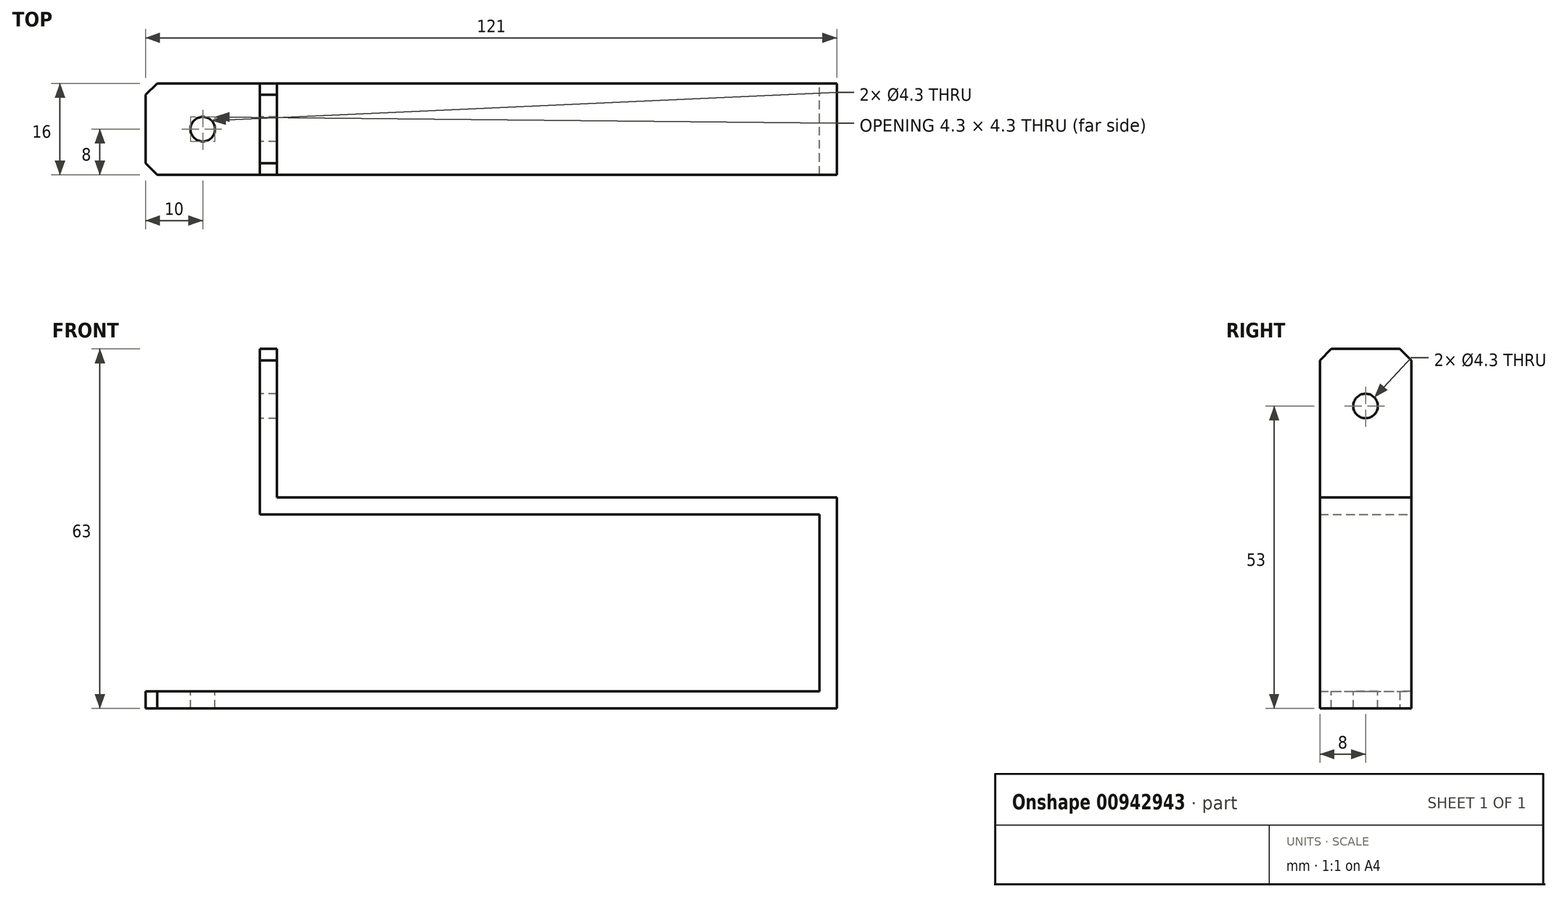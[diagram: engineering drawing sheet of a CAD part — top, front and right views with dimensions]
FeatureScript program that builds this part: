
annotation { "Feature Type Name" : "Feature", "Feature Type Description" : "" }
export const myFeature = defineFeature(function(context is Context, id is Id, definition is map)
    precondition{}
    {
        {
            var Q0;
            Q0=qCreatedBy(makeId("Front.planeOp"),FACE);
            var sketch = newSketch(context, id + "F0", { "sketchPlane" : qUnion([Q0])});
            skLineSegment(sketch, "E0", {"start": v(0, 0) * mm, "end": v(-20, 0) * mm});
            skLineSegment(sketch, "E1", {"start": v(0, 0) * mm, "end": v(0, 60) * mm, "construction": true});
            skPoint(sketch, "E2", {"position": v(-10, 0) * mm});
            skPoint(sketch, "E3", {"position": v(0, 50) * mm});
            skLineSegment(sketch, "E4", {"start": v(0, 0) * mm, "end": v(0, 31) * mm, "construction": true});
            skLineSegment(sketch, "E5", {"start": v(0, 31) * mm, "end": v(98, 31) * mm});
            skLineSegment(sketch, "E6", {"start": v(98, 31) * mm, "end": v(98, 0) * mm});
            skLineSegment(sketch, "E7", {"start": v(98, 0) * mm, "end": v(0, 0) * mm});
            skLineSegment(sketch, "E8.0", {"start": v(101, -3) * mm, "end": v(0, -3) * mm});
            skLineSegment(sketch, "E8.1", {"start": v(101, 34) * mm, "end": v(101, -3) * mm});
            skLineSegment(sketch, "E8.2", {"start": v(3, 34) * mm, "end": v(101, 34) * mm});
            skLineSegment(sketch, "E9", {"start": v(0, -3) * mm, "end": v(-20, -3) * mm});
            skLineSegment(sketch, "E10", {"start": v(-20, -3) * mm, "end": v(-20, 0) * mm});
            skLineSegment(sketch, "E11", {"start": v(3, 34) * mm, "end": v(3, 60) * mm});
            skLineSegment(sketch, "E12", {"start": v(3, 60) * mm, "end": v(0, 60) * mm});
            skLineSegment(sketch, "E13", {"start": v(0, 31) * mm, "end": v(0, 60) * mm});
            skSolve(sketch);
        }
        {
            var Q0;
            Q0 = qSketchRegion(id + "F0", true);
            extrude(context, id + "F1", {"entities" : qUnion([Q0]), "depth" : 16 * mm, "offsetDistance" : 25 * mm});
        }
        {
            var Q0;
            Q0=makeQuery(id+"F1.opExtrude","SWEPT_FACE",FACE,{"disambiguationData":[OSD([sQuery(id+"F0.wireOp",EDGE,"E0"),sQuery(id+"F0.wireOp",EDGE,"E7")])]});
            var sketch = newSketch(context, id + "F2", { "sketchPlane" : qUnion([Q0])});
            skPoint(sketch, "E14", {"position": v(-20, -8) * mm});
            skCircle(sketch, "E15", {"center": v(-10, -8) * mm, "radius": 2.15 * mm});
            skSolve(sketch);
        }
        {
            var Q0;
            Q0 = qSketchRegion(id + "F2", true);
            extrude(context, id + "F3", {"entities" : qUnion([Q0]), "operationType" : NewBodyOperationType.REMOVE, "oppositeDirection" : true, "depth" : 25 * mm, "offsetDistance" : 25 * mm});
        }
        {
            var Q0;
            Q0=makeQuery(id+"F1.opExtrude","SWEPT_FACE",FACE,{"disambiguationData":[OSD([sQuery(id+"F0.wireOp",EDGE,"E13")])]});
            var sketch = newSketch(context, id + "F4", { "sketchPlane" : qUnion([Q0])});
            skPoint(sketch, "E16", {"position": v(8, 60) * mm});
            skCircle(sketch, "E17", {"center": v(8, 50) * mm, "radius": 2.15 * mm});
            skCircle(sketch, "E18", {"center": v(8, 50) * mm, "radius": 4 * mm});
            skSolve(sketch);
        }
        {
            var Q0;
            Q0=makeQuery(id+"F4.imprint","IMPRINT",FACE,{"disambiguationData":[TD([[makeQuery(id+"F4.imprint","IMPRINT",EDGE,{"derivedFrom":sQuery(id+"F4.wireOp",EDGE,"E17")}),1.0]])]});
            extrude(context, id + "F5", {"entities" : qUnion([Q0]), "operationType" : NewBodyOperationType.REMOVE, "oppositeDirection" : true, "depth" : 25 * mm, "offsetDistance" : 25 * mm});
        }
        {
            var Q0;
            Q0=makeQuery(id+"F1.opExtrude","CAP_EDGE",EDGE,{"disambiguationData":[OSD([sQuery(id+"F0.wireOp",EDGE,"E12")])],"isStart":false});
            var Q1;
            Q1=makeQuery(id+"F1.opExtrude","CAP_EDGE",EDGE,{"disambiguationData":[OSD([sQuery(id+"F0.wireOp",EDGE,"E12")])],"isStart":true});
            var Q2;
            Q2=makeQuery(id+"F1.opExtrude","CAP_EDGE",EDGE,{"disambiguationData":[OSD([sQuery(id+"F0.wireOp",EDGE,"E10")])],"isStart":false});
            var Q3;
            Q3=makeQuery(id+"F1.opExtrude","CAP_EDGE",EDGE,{"disambiguationData":[OSD([sQuery(id+"F0.wireOp",EDGE,"E10")])],"isStart":true});
            chamfer(context, id + "F6", {"entities" : qUnion([Q0, Q1, Q2, Q3]), "width" : 2 * mm, "tangentPropagation" : true});
        }
    });
